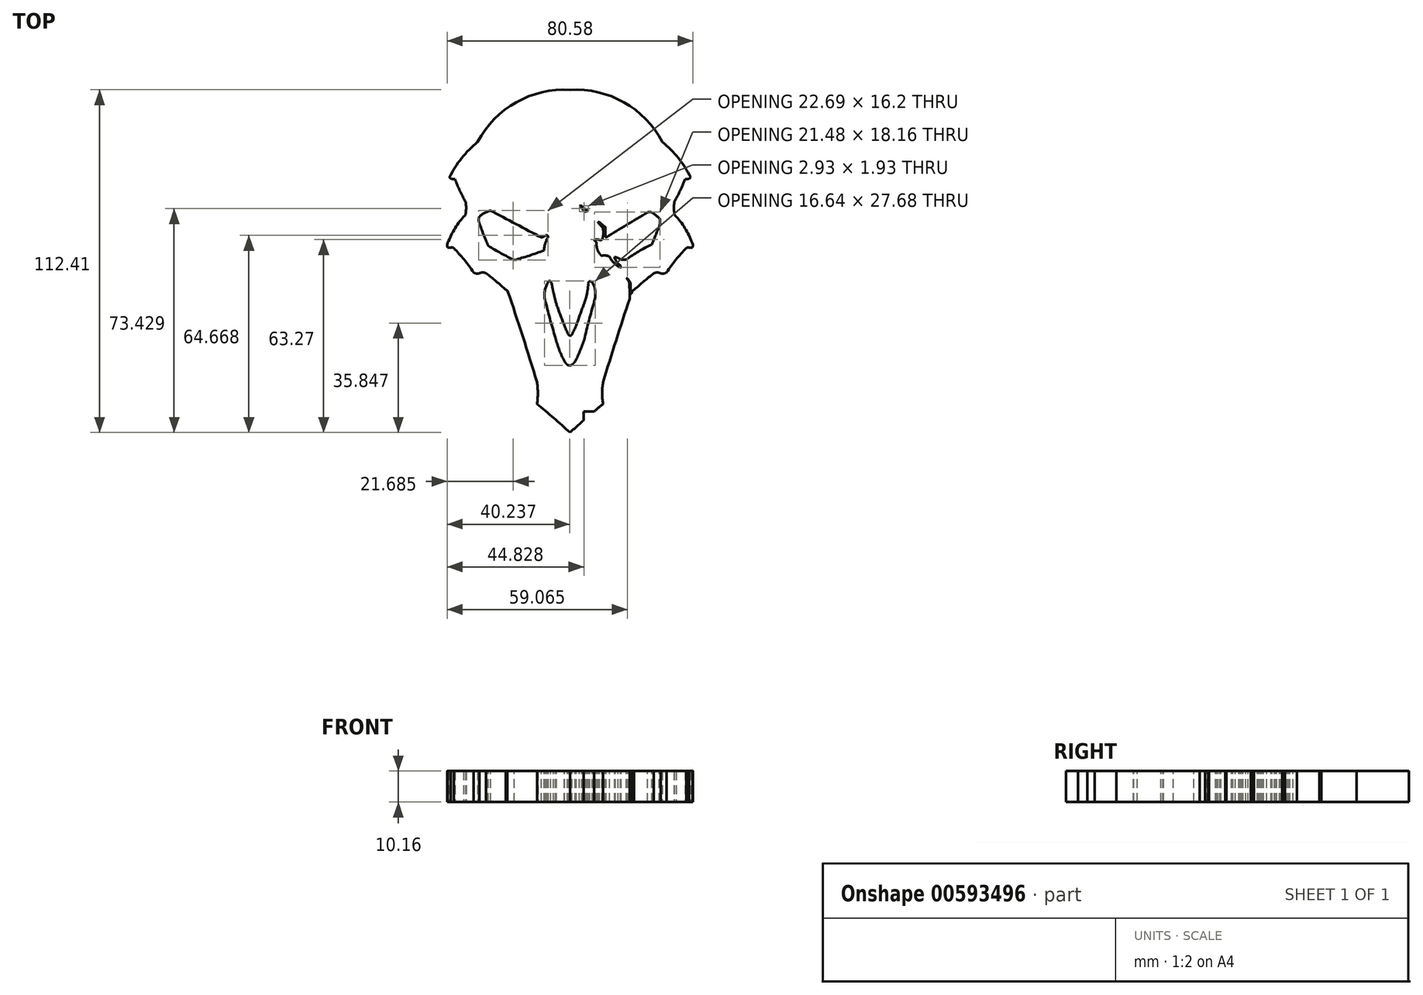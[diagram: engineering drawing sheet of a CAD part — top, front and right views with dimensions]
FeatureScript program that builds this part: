
annotation { "Feature Type Name" : "Feature", "Feature Type Description" : "" }
export const myFeature = defineFeature(function(context is Context, id is Id, definition is map)
    precondition{}
    {
        {
            var Q0;
            Q0=qCreatedBy(makeId("Top.planeOp"),FACE);
            var sketch = newSketch(context, id + "F0", { "sketchPlane" : qUnion([Q0])});
            skArc(sketch, "E0", {"start": v(-30.27, 46.68) * mm, "mid": v(-35.53, 41.4) * mm, "end": v(-39.5, 35.1) * mm});
            skArc(sketch, "E1", {"start": v(-39.5, 35.1) * mm, "mid": v(-38.7, 34.53) * mm, "end": v(-37.73, 34.53) * mm});
            skArc(sketch, "E2", {"start": v(-37.73, 34.53) * mm, "mid": v(-36.12, 30.74) * mm, "end": v(-34.24, 27.07) * mm});
            skArc(sketch, "E3", {"start": v(-34.24, 23.12) * mm, "mid": v(-34.05, 25.1) * mm, "end": v(-34.24, 27.07) * mm});
            skArc(sketch, "E4", {"start": v(-34.86, 22.24) * mm, "mid": v(-34.4, 22.58) * mm, "end": v(-34.24, 23.12) * mm});
            skArc(sketch, "E5", {"start": v(-38.1, 11.91) * mm, "mid": v(-38.57, 12.1) * mm, "end": v(-39.06, 12.04) * mm});
            skArc(sketch, "E6", {"start": v(-31.65, 3.94) * mm, "mid": v(-34.7, 8.07) * mm, "end": v(-38.1, 11.91) * mm});
            skArc(sketch, "E7", {"start": v(-34.86, 22.24) * mm, "mid": v(-38, 17.87) * mm, "end": v(-40.29, 12.99) * mm});
            skArc(sketch, "E8", {"start": v(-40.29, 12.99) * mm, "mid": v(-40.25, 12.5) * mm, "end": v(-40.1, 12.04) * mm});
            skArc(sketch, "E9", {"start": v(-40.1, 12.04) * mm, "mid": v(-39.58, 12.03) * mm, "end": v(-39.06, 12.04) * mm});
            skArc(sketch, "E10", {"start": v(-31.65, 3.94) * mm, "mid": v(-30.7, 3.53) * mm, "end": v(-29.68, 3.65) * mm});
            skArc(sketch, "E11", {"start": v(-27.5, 3.65) * mm, "mid": v(-28.59, 3.9) * mm, "end": v(-29.68, 3.65) * mm});
            skArc(sketch, "E12", {"start": v(-21.02, -1.81) * mm, "mid": v(-24.21, 0.97) * mm, "end": v(-27.5, 3.65) * mm});
            skArc(sketch, "E13", {"start": v(-20.5, -2.08) * mm, "mid": v(-20.73, -1.9) * mm, "end": v(-21.02, -1.81) * mm});
            skArc(sketch, "E14", {"start": v(-10.83, -32.15) * mm, "mid": v(-15.5, -17.06) * mm, "end": v(-20.5, -2.08) * mm});
            skArc(sketch, "E15", {"start": v(-10.83, -39.22) * mm, "mid": v(-10.55, -35.68) * mm, "end": v(-10.83, -32.15) * mm});
            skArc(sketch, "E16", {"start": v(0, -48.6) * mm, "mid": v(-5.35, -43.82) * mm, "end": v(-10.83, -39.22) * mm});
            skLineSegment(sketch, "E17", {"start": v(0, 63.77) * mm, "end": v(0, -48.6) * mm});
            skArc(sketch, "E18", {"start": v(0, 63.77) * mm, "mid": v(-17.65, 59.68) * mm, "end": v(-30.27, 46.68) * mm});
            skSolve(sketch);
        }
        {
            var Q0;
            Q0 = qSketchRegion(id + "F0", true);
            extrude(context, id + "F1", {"entities" : qUnion([Q0]), "depth" : 10.16 * mm, "offsetDistance" : 25.4 * mm});
        }
        {
            var Q0;
            Q0=makeQuery(id+"F1.opExtrude","SWEPT_BODY",BODY,{"disambiguationData":[OSD([sQuery(id+"F0.wireOp",EDGE,"E0"),sQuery(id+"F0.wireOp",EDGE,"E1"),sQuery(id+"F0.wireOp",EDGE,"E2"),sQuery(id+"F0.wireOp",EDGE,"E3"),sQuery(id+"F0.wireOp",EDGE,"E4"),sQuery(id+"F0.wireOp",EDGE,"E5"),sQuery(id+"F0.wireOp",EDGE,"E6"),sQuery(id+"F0.wireOp",EDGE,"E7"),sQuery(id+"F0.wireOp",EDGE,"E8"),sQuery(id+"F0.wireOp",EDGE,"E9"),sQuery(id+"F0.wireOp",EDGE,"E10"),sQuery(id+"F0.wireOp",EDGE,"E11"),sQuery(id+"F0.wireOp",EDGE,"E12"),sQuery(id+"F0.wireOp",EDGE,"E13"),sQuery(id+"F0.wireOp",EDGE,"E14"),sQuery(id+"F0.wireOp",EDGE,"E15"),sQuery(id+"F0.wireOp",EDGE,"E16"),sQuery(id+"F0.wireOp",EDGE,"E17"),sQuery(id+"F0.wireOp",EDGE,"E18")])]});
            var Q1;
            Q1=qCreatedBy(makeId("Right.planeOp"),FACE);
            mirror(context, id + "F2", {"operationType" : NewBodyOperationType.ADD, "entities" : qUnion([Q0]), "mirrorPlane" : qUnion([Q1])});
        }
        {
            var Q0;
            {var subQ0=makeQuery(id+"F1.opExtrude","CAP_FACE",FACE,{"disambiguationData":[OSD([sQuery(id+"F0.wireOp",EDGE,"E0"),sQuery(id+"F0.wireOp",EDGE,"E1"),sQuery(id+"F0.wireOp",EDGE,"E2"),sQuery(id+"F0.wireOp",EDGE,"E3"),sQuery(id+"F0.wireOp",EDGE,"E4"),sQuery(id+"F0.wireOp",EDGE,"E5"),sQuery(id+"F0.wireOp",EDGE,"E6"),sQuery(id+"F0.wireOp",EDGE,"E7"),sQuery(id+"F0.wireOp",EDGE,"E8"),sQuery(id+"F0.wireOp",EDGE,"E9"),sQuery(id+"F0.wireOp",EDGE,"E10"),sQuery(id+"F0.wireOp",EDGE,"E11"),sQuery(id+"F0.wireOp",EDGE,"E12"),sQuery(id+"F0.wireOp",EDGE,"E13"),sQuery(id+"F0.wireOp",EDGE,"E14"),sQuery(id+"F0.wireOp",EDGE,"E15"),sQuery(id+"F0.wireOp",EDGE,"E16"),sQuery(id+"F0.wireOp",EDGE,"E17"),sQuery(id+"F0.wireOp",EDGE,"E18")])],"isStart":false});Q0=makeQuery(id+"F2.boolean.opBoolean","MERGE",FACE,{"derivedFrom":[subQ0,makeQuery(id+"F2.opPattern","COPY",FACE,{"derivedFrom":subQ0,"instanceName":"1"})]});}
            var sketch = newSketch(context, id + "F3", { "sketchPlane" : qUnion([Q0])});
            skArc(sketch, "E19", {"start": v(-26, 24.18) * mm, "mid": v(-17.72, 19.77) * mm, "end": v(-9.44, 15.37) * mm});
            skArc(sketch, "E20", {"start": v(-9.44, 15.37) * mm, "mid": v(-8.67, 15.65) * mm, "end": v(-7.94, 16.04) * mm});
            skArc(sketch, "E21", {"start": v(-26.76, 12.61) * mm, "mid": v(-22.58, 10.17) * mm, "end": v(-18.26, 7.98) * mm});
            skArc(sketch, "E22", {"start": v(-29.69, 20.03) * mm, "mid": v(-28.33, 16.28) * mm, "end": v(-26.76, 12.61) * mm});
            skArc(sketch, "E23", {"start": v(-29.69, 22.27) * mm, "mid": v(-29.95, 21.15) * mm, "end": v(-29.69, 20.03) * mm});
            skArc(sketch, "E24", {"start": v(-26, 24.18) * mm, "mid": v(-27.96, 23.44) * mm, "end": v(-29.69, 22.27) * mm});
            skArc(sketch, "E25", {"start": v(-7.58, 16.16) * mm, "mid": v(-7.77, 16.1) * mm, "end": v(-7.94, 16.04) * mm});
            skArc(sketch, "E26", {"start": v(-7.58, 16.16) * mm, "mid": v(-7.47, 16.14) * mm, "end": v(-7.35, 16.16) * mm});
            skArc(sketch, "E27", {"start": v(-7.28, 15.37) * mm, "mid": v(-7.26, 15.77) * mm, "end": v(-7.35, 16.16) * mm});
            skArc(sketch, "E28", {"start": v(-7.28, 15.37) * mm, "mid": v(-8.16, 13.31) * mm, "end": v(-8.55, 11.1) * mm});
            skArc(sketch, "E29", {"start": v(-18.26, 7.98) * mm, "mid": v(-13.36, 9.42) * mm, "end": v(-8.55, 11.1) * mm});
            skSolve(sketch);
        }
        {
            var Q0;
            Q0 = qSketchRegion(id + "F3", true);
            extrude(context, id + "F4", {"entities" : qUnion([Q0]), "operationType" : NewBodyOperationType.REMOVE, "oppositeDirection" : true, "depth" : 25.4 * mm, "offsetDistance" : 25.4 * mm});
        }
        {
            var Q0;
            {var subQ0=makeQuery(id+"F1.opExtrude","CAP_FACE",FACE,{"disambiguationData":[OSD([sQuery(id+"F0.wireOp",EDGE,"E0"),sQuery(id+"F0.wireOp",EDGE,"E1"),sQuery(id+"F0.wireOp",EDGE,"E2"),sQuery(id+"F0.wireOp",EDGE,"E3"),sQuery(id+"F0.wireOp",EDGE,"E4"),sQuery(id+"F0.wireOp",EDGE,"E5"),sQuery(id+"F0.wireOp",EDGE,"E6"),sQuery(id+"F0.wireOp",EDGE,"E7"),sQuery(id+"F0.wireOp",EDGE,"E8"),sQuery(id+"F0.wireOp",EDGE,"E9"),sQuery(id+"F0.wireOp",EDGE,"E10"),sQuery(id+"F0.wireOp",EDGE,"E11"),sQuery(id+"F0.wireOp",EDGE,"E12"),sQuery(id+"F0.wireOp",EDGE,"E13"),sQuery(id+"F0.wireOp",EDGE,"E14"),sQuery(id+"F0.wireOp",EDGE,"E15"),sQuery(id+"F0.wireOp",EDGE,"E16"),sQuery(id+"F0.wireOp",EDGE,"E17"),sQuery(id+"F0.wireOp",EDGE,"E18")])],"isStart":false});Q0=makeQuery(id+"F2.boolean.opBoolean","MERGE",FACE,{"derivedFrom":[subQ0,makeQuery(id+"F2.opPattern","COPY",FACE,{"derivedFrom":subQ0,"instanceName":"1"})]});}
            var sketch = newSketch(context, id + "F5", { "sketchPlane" : qUnion([Q0])});
            skArc(sketch, "E30", {"start": v(25.42, 23.61) * mm, "mid": v(18.6, 19.55) * mm, "end": v(11.87, 15.37) * mm});
            skArc(sketch, "E31", {"start": v(26.78, 23.61) * mm, "mid": v(26.1, 23.76) * mm, "end": v(25.42, 23.61) * mm});
            skArc(sketch, "E32", {"start": v(29.26, 21.73) * mm, "mid": v(28.05, 22.71) * mm, "end": v(26.78, 23.61) * mm});
            skArc(sketch, "E33", {"start": v(29.5, 21.39) * mm, "mid": v(29.4, 21.57) * mm, "end": v(29.26, 21.73) * mm});
            skArc(sketch, "E34", {"start": v(29.5, 19.76) * mm, "mid": v(29.51, 20.58) * mm, "end": v(29.5, 21.39) * mm});
            skArc(sketch, "E35", {"start": v(26.78, 13.08) * mm, "mid": v(28.17, 16.4) * mm, "end": v(29.5, 19.76) * mm});
            skArc(sketch, "E36", {"start": v(26.78, 13.08) * mm, "mid": v(22.49, 10.8) * mm, "end": v(18.43, 8.13) * mm});
            skArc(sketch, "E37", {"start": v(16.8, 8.13) * mm, "mid": v(17.62, 8.07) * mm, "end": v(18.43, 8.13) * mm});
            skArc(sketch, "E38", {"start": v(16.8, 8.13) * mm, "mid": v(15.76, 8.64) * mm, "end": v(14.65, 8.96) * mm});
            skArc(sketch, "E39", {"start": v(12.98, 9) * mm, "mid": v(13.7, 7.88) * mm, "end": v(14.58, 6.88) * mm});
            skArc(sketch, "E40", {"start": v(12.1, 9.4) * mm, "mid": v(11.24, 9.46) * mm, "end": v(10.38, 9.4) * mm});
            skArc(sketch, "E41", {"start": v(9.5, 10.35) * mm, "mid": v(9.88, 9.82) * mm, "end": v(10.38, 9.4) * mm});
            skArc(sketch, "E42", {"start": v(8.7, 13.2) * mm, "mid": v(8.88, 11.72) * mm, "end": v(9.5, 10.35) * mm});
            skArc(sketch, "E43", {"start": v(8.7, 13.2) * mm, "mid": v(8.63, 13.72) * mm, "end": v(8.25, 14.08) * mm});
            skArc(sketch, "E44", {"start": v(8.07, 14.36) * mm, "mid": v(8.15, 14.2) * mm, "end": v(8.25, 14.08) * mm});
            skArc(sketch, "E45", {"start": v(8.07, 14.73) * mm, "mid": v(8.03, 14.54) * mm, "end": v(8.07, 14.36) * mm});
            skArc(sketch, "E46", {"start": v(14.9, 8.09) * mm, "mid": v(15.57, 7) * mm, "end": v(16.55, 6.16) * mm});
            skArc(sketch, "E47", {"start": v(16.55, 6.16) * mm, "mid": v(16.6, 5.84) * mm, "end": v(16.84, 5.6) * mm});
            skArc(sketch, "E48", {"start": v(15.76, 5.9) * mm, "mid": v(16.27, 5.66) * mm, "end": v(16.84, 5.6) * mm});
            skArc(sketch, "E49", {"start": v(14.58, 6.88) * mm, "mid": v(15.14, 6.35) * mm, "end": v(15.76, 5.9) * mm});
            skArc(sketch, "E50", {"start": v(10.45, 14.6) * mm, "mid": v(10.58, 14.76) * mm, "end": v(10.64, 14.94) * mm});
            skArc(sketch, "E51", {"start": v(10.64, 14.94) * mm, "mid": v(10.87, 16.03) * mm, "end": v(10.9, 17.14) * mm});
            skArc(sketch, "E52", {"start": v(10.9, 17.14) * mm, "mid": v(10.85, 17.89) * mm, "end": v(10.64, 18.61) * mm});
            skArc(sketch, "E53", {"start": v(10.64, 18.61) * mm, "mid": v(10, 19.4) * mm, "end": v(9.28, 20.13) * mm});
            skArc(sketch, "E54", {"start": v(9.2, 20.42) * mm, "mid": v(9.22, 20.27) * mm, "end": v(9.28, 20.13) * mm});
            skArc(sketch, "E55", {"start": v(9.2, 20.42) * mm, "mid": v(9.46, 20.35) * mm, "end": v(9.72, 20.42) * mm});
            skArc(sketch, "E56", {"start": v(9.72, 20.42) * mm, "mid": v(10.53, 19.58) * mm, "end": v(11.48, 18.92) * mm});
            skArc(sketch, "E57", {"start": v(11.59, 18.76) * mm, "mid": v(11.55, 18.85) * mm, "end": v(11.48, 18.92) * mm});
            skArc(sketch, "E58", {"start": v(11.74, 15.48) * mm, "mid": v(11.78, 15.4) * mm, "end": v(11.87, 15.37) * mm});
            skArc(sketch, "E59", {"start": v(11.59, 18.76) * mm, "mid": v(11.54, 17.12) * mm, "end": v(11.74, 15.48) * mm});
            skArc(sketch, "E60", {"start": v(9.51, 14.6) * mm, "mid": v(9.98, 14.5) * mm, "end": v(10.45, 14.6) * mm});
            skArc(sketch, "E61", {"start": v(9.51, 14.6) * mm, "mid": v(9.27, 14.67) * mm, "end": v(9.02, 14.7) * mm});
            skArc(sketch, "E62", {"start": v(8.48, 14.71) * mm, "mid": v(8.75, 14.65) * mm, "end": v(9.02, 14.7) * mm});
            skArc(sketch, "E63", {"start": v(8.07, 14.73) * mm, "mid": v(8.27, 14.69) * mm, "end": v(8.48, 14.71) * mm});
            skArc(sketch, "E64", {"start": v(14.65, 8.96) * mm, "mid": v(14.6, 8.78) * mm, "end": v(14.65, 8.6) * mm});
            skArc(sketch, "E65", {"start": v(14.65, 8.6) * mm, "mid": v(14.76, 8.34) * mm, "end": v(14.9, 8.09) * mm});
            skArc(sketch, "E66", {"start": v(12.98, 9) * mm, "mid": v(12.57, 9.26) * mm, "end": v(12.1, 9.4) * mm});
            skSolve(sketch);
        }
        {
            var Q0;
            Q0 = qSketchRegion(id + "F5", true);
            extrude(context, id + "F6", {"entities" : qUnion([Q0]), "operationType" : NewBodyOperationType.REMOVE, "oppositeDirection" : true, "depth" : 25.4 * mm, "offsetDistance" : 25.4 * mm});
        }
        {
            var Q0;
            Q0 = qSketchRegion(id + "F5", true);
            extrude(context, id + "F7", {"entities" : qUnion([Q0]), "operationType" : NewBodyOperationType.REMOVE, "oppositeDirection" : true, "depth" : 25.4 * mm, "offsetDistance" : 25.4 * mm});
        }
        {
            var Q0;
            {var subQ0=makeQuery(id+"F1.opExtrude","CAP_FACE",FACE,{"disambiguationData":[OSD([sQuery(id+"F0.wireOp",EDGE,"E0"),sQuery(id+"F0.wireOp",EDGE,"E1"),sQuery(id+"F0.wireOp",EDGE,"E2"),sQuery(id+"F0.wireOp",EDGE,"E3"),sQuery(id+"F0.wireOp",EDGE,"E4"),sQuery(id+"F0.wireOp",EDGE,"E5"),sQuery(id+"F0.wireOp",EDGE,"E6"),sQuery(id+"F0.wireOp",EDGE,"E7"),sQuery(id+"F0.wireOp",EDGE,"E8"),sQuery(id+"F0.wireOp",EDGE,"E9"),sQuery(id+"F0.wireOp",EDGE,"E10"),sQuery(id+"F0.wireOp",EDGE,"E11"),sQuery(id+"F0.wireOp",EDGE,"E12"),sQuery(id+"F0.wireOp",EDGE,"E13"),sQuery(id+"F0.wireOp",EDGE,"E14"),sQuery(id+"F0.wireOp",EDGE,"E15"),sQuery(id+"F0.wireOp",EDGE,"E16"),sQuery(id+"F0.wireOp",EDGE,"E17"),sQuery(id+"F0.wireOp",EDGE,"E18")])],"isStart":false});Q0=makeQuery(id+"F2.boolean.opBoolean","MERGE",FACE,{"derivedFrom":[subQ0,makeQuery(id+"F2.opPattern","COPY",FACE,{"derivedFrom":subQ0,"instanceName":"1"})]});}
            var sketch = newSketch(context, id + "F8", { "sketchPlane" : qUnion([Q0])});
            skArc(sketch, "E67", {"start": v(19.58, -4.75) * mm, "mid": v(19.54, -2.14) * mm, "end": v(19.42, 0.46) * mm});
            skArc(sketch, "E68", {"start": v(19.42, 0.46) * mm, "mid": v(19.15, 1.16) * mm, "end": v(18.68, 1.76) * mm});
            skArc(sketch, "E69", {"start": v(18.68, 2) * mm, "mid": v(18.66, 1.88) * mm, "end": v(18.68, 1.76) * mm});
            skArc(sketch, "E70", {"start": v(18.75, 2.17) * mm, "mid": v(18.7, 2.1) * mm, "end": v(18.68, 2) * mm});
            skArc(sketch, "E71", {"start": v(18.75, 2.17) * mm, "mid": v(18.8, 1.91) * mm, "end": v(19, 1.74) * mm});
            skArc(sketch, "E72", {"start": v(19.78, 0.52) * mm, "mid": v(19.41, 1.15) * mm, "end": v(19, 1.74) * mm});
            skArc(sketch, "E73", {"start": v(19.78, 0.52) * mm, "mid": v(19.85, -1.26) * mm, "end": v(20.03, -3.02) * mm});
            skArc(sketch, "E74", {"start": v(20.03, -3.02) * mm, "mid": v(20.05, -3.06) * mm, "end": v(20.08, -3.08) * mm});
            skArc(sketch, "E75", {"start": v(20.08, -3.08) * mm, "mid": v(20.16, -3.07) * mm, "end": v(20.22, -3) * mm});
            skArc(sketch, "E76", {"start": v(19.58, -4.75) * mm, "mid": v(24.58, -5.6) * mm, "end": v(20.22, -3) * mm});
            skSolve(sketch);
        }
        {
            var Q0;
            {var subQ0=makeQuery(id+"F1.opExtrude","CAP_FACE",FACE,{"disambiguationData":[OSD([sQuery(id+"F0.wireOp",EDGE,"E0"),sQuery(id+"F0.wireOp",EDGE,"E1"),sQuery(id+"F0.wireOp",EDGE,"E2"),sQuery(id+"F0.wireOp",EDGE,"E3"),sQuery(id+"F0.wireOp",EDGE,"E4"),sQuery(id+"F0.wireOp",EDGE,"E5"),sQuery(id+"F0.wireOp",EDGE,"E6"),sQuery(id+"F0.wireOp",EDGE,"E7"),sQuery(id+"F0.wireOp",EDGE,"E8"),sQuery(id+"F0.wireOp",EDGE,"E9"),sQuery(id+"F0.wireOp",EDGE,"E10"),sQuery(id+"F0.wireOp",EDGE,"E11"),sQuery(id+"F0.wireOp",EDGE,"E12"),sQuery(id+"F0.wireOp",EDGE,"E13"),sQuery(id+"F0.wireOp",EDGE,"E14"),sQuery(id+"F0.wireOp",EDGE,"E15"),sQuery(id+"F0.wireOp",EDGE,"E16"),sQuery(id+"F0.wireOp",EDGE,"E17"),sQuery(id+"F0.wireOp",EDGE,"E18")])],"isStart":false});Q0=makeQuery(id+"F2.boolean.opBoolean","MERGE",FACE,{"derivedFrom":[subQ0,makeQuery(id+"F2.opPattern","COPY",FACE,{"derivedFrom":subQ0,"instanceName":"1"})]});}
            var sketch = newSketch(context, id + "F9", { "sketchPlane" : qUnion([Q0])});
            skArc(sketch, "E77", {"start": v(3.88, 25.76) * mm, "mid": v(4.36, 25.2) * mm, "end": v(4.93, 24.73) * mm});
            skArc(sketch, "E78", {"start": v(4.93, 24.73) * mm, "mid": v(5.45, 24.54) * mm, "end": v(6, 24.5) * mm});
            skArc(sketch, "E79", {"start": v(4.68, 23.9) * mm, "mid": v(4.97, 23.88) * mm, "end": v(5.26, 23.9) * mm});
            skArc(sketch, "E80", {"start": v(4.68, 23.9) * mm, "mid": v(3.93, 24.9) * mm, "end": v(3.07, 25.8) * mm});
            skArc(sketch, "E81", {"start": v(3.07, 25.8) * mm, "mid": v(3.47, 25.74) * mm, "end": v(3.88, 25.76) * mm});
            skArc(sketch, "E82", {"start": v(6, 24.5) * mm, "mid": v(5.8, 24.24) * mm, "end": v(5.69, 23.95) * mm});
            skArc(sketch, "E83", {"start": v(5.69, 23.95) * mm, "mid": v(5.47, 23.94) * mm, "end": v(5.26, 23.9) * mm});
            skSolve(sketch);
        }
        {
            var Q0;
            Q0 = qSketchRegion(id + "F9", true);
            extrude(context, id + "F10", {"entities" : qUnion([Q0]), "operationType" : NewBodyOperationType.REMOVE, "oppositeDirection" : true, "depth" : 25.4 * mm, "offsetDistance" : 25.4 * mm});
        }
        {
            var Q0;
            {var subQ20=sQuery(id+"F8.wireOp",EDGE,"E67");Q0=makeQuery(id+"F8.imprint","IMPRINT",FACE,{"disambiguationData":[TD([[makeQuery(id+"F8.imprint","IMPRINT",EDGE,{"derivedFrom":subQ20}),1.0]])]});}
            var sketch = newSketch(context, id + "F11", { "sketchPlane" : qUnion([Q0])});
            skArc(sketch, "E84", {"start": v(-6.35, 0.89) * mm, "mid": v(-6.69, 1.1) * mm, "end": v(-7.05, 0.93) * mm});
            skArc(sketch, "E85", {"start": v(-7.05, 0.93) * mm, "mid": v(-8.21, -1.83) * mm, "end": v(-8.25, -4.82) * mm});
            skArc(sketch, "E86", {"start": v(-8.25, -4.82) * mm, "mid": v(-6.62, -11.16) * mm, "end": v(-4.78, -17.44) * mm});
            skArc(sketch, "E87", {"start": v(-4.78, -17.44) * mm, "mid": v(-3.54, -21.47) * mm, "end": v(-1.75, -25.28) * mm});
            skArc(sketch, "E88", {"start": v(-1.75, -25.28) * mm, "mid": v(-1.37, -25.86) * mm, "end": v(-0.9, -26.35) * mm});
            skArc(sketch, "E89", {"start": v(-0.9, -26.35) * mm, "mid": v(-0.13, -26.59) * mm, "end": v(0.64, -26.35) * mm});
            skArc(sketch, "E90", {"start": v(0.64, -26.35) * mm, "mid": v(1.2, -25.84) * mm, "end": v(1.7, -25.28) * mm});
            skArc(sketch, "E91", {"start": v(1.7, -25.28) * mm, "mid": v(3.44, -21.43) * mm, "end": v(4.85, -17.44) * mm});
            skArc(sketch, "E92", {"start": v(8.19, -4.82) * mm, "mid": v(6.4, -11.1) * mm, "end": v(4.85, -17.44) * mm});
            skArc(sketch, "E93", {"start": v(8.19, -4.82) * mm, "mid": v(8.27, -3.16) * mm, "end": v(8.19, -1.5) * mm});
            skArc(sketch, "E94", {"start": v(8.19, -1.5) * mm, "mid": v(7.82, -0.38) * mm, "end": v(7.27, 0.67) * mm});
            skArc(sketch, "E95", {"start": v(7.27, 0.67) * mm, "mid": v(6.93, 0.9) * mm, "end": v(6.55, 1.01) * mm});
            skArc(sketch, "E96", {"start": v(5.65, -2.47) * mm, "mid": v(5.9, -1.06) * mm, "end": v(5.93, 0.36) * mm});
            skArc(sketch, "E97", {"start": v(4.5, -6.68) * mm, "mid": v(5.18, -4.6) * mm, "end": v(5.65, -2.47) * mm});
            skArc(sketch, "E98", {"start": v(4.5, -6.68) * mm, "mid": v(3.23, -10.02) * mm, "end": v(2.08, -13.4) * mm});
            skArc(sketch, "E99", {"start": v(0.57, -16.55) * mm, "mid": v(1.35, -14.98) * mm, "end": v(2.08, -13.4) * mm});
            skArc(sketch, "E100", {"start": v(-0.45, -16.55) * mm, "mid": v(0.06, -16.81) * mm, "end": v(0.57, -16.55) * mm});
            skArc(sketch, "E101", {"start": v(-1.88, -13.4) * mm, "mid": v(-1.23, -15) * mm, "end": v(-0.45, -16.55) * mm});
            skArc(sketch, "E102", {"start": v(-4.4, -6.68) * mm, "mid": v(-3.18, -10.05) * mm, "end": v(-1.88, -13.4) * mm});
            skArc(sketch, "E103", {"start": v(-5.5, -2.47) * mm, "mid": v(-4.97, -4.58) * mm, "end": v(-4.4, -6.68) * mm});
            skArc(sketch, "E104", {"start": v(-5.97, -0.02) * mm, "mid": v(-5.74, -1.24) * mm, "end": v(-5.5, -2.47) * mm});
            skArc(sketch, "E105", {"start": v(-5.97, -0.02) * mm, "mid": v(-6.1, 0.46) * mm, "end": v(-6.35, 0.89) * mm});
            skArc(sketch, "E106", {"start": v(6.55, 1.01) * mm, "mid": v(6.15, 0.77) * mm, "end": v(5.93, 0.36) * mm});
            skSolve(sketch);
        }
        {
            var Q0;
            Q0 = qSketchRegion(id + "F11", true);
            extrude(context, id + "F12", {"entities" : qUnion([Q0]), "operationType" : NewBodyOperationType.REMOVE, "oppositeDirection" : true, "depth" : 25.4 * mm, "offsetDistance" : 25.4 * mm});
        }
        {
            var Q0;
            {var subQ0=makeQuery(id+"F1.opExtrude","CAP_FACE",FACE,{"disambiguationData":[OSD([sQuery(id+"F0.wireOp",EDGE,"E0"),sQuery(id+"F0.wireOp",EDGE,"E1"),sQuery(id+"F0.wireOp",EDGE,"E2"),sQuery(id+"F0.wireOp",EDGE,"E3"),sQuery(id+"F0.wireOp",EDGE,"E4"),sQuery(id+"F0.wireOp",EDGE,"E5"),sQuery(id+"F0.wireOp",EDGE,"E6"),sQuery(id+"F0.wireOp",EDGE,"E7"),sQuery(id+"F0.wireOp",EDGE,"E8"),sQuery(id+"F0.wireOp",EDGE,"E9"),sQuery(id+"F0.wireOp",EDGE,"E10"),sQuery(id+"F0.wireOp",EDGE,"E11"),sQuery(id+"F0.wireOp",EDGE,"E12"),sQuery(id+"F0.wireOp",EDGE,"E13"),sQuery(id+"F0.wireOp",EDGE,"E14"),sQuery(id+"F0.wireOp",EDGE,"E15"),sQuery(id+"F0.wireOp",EDGE,"E16"),sQuery(id+"F0.wireOp",EDGE,"E17"),sQuery(id+"F0.wireOp",EDGE,"E18")])],"isStart":false});Q0=makeQuery(id+"F2.boolean.opBoolean","MERGE",FACE,{"derivedFrom":[subQ0,makeQuery(id+"F2.opPattern","COPY",FACE,{"derivedFrom":subQ0,"instanceName":"1"})]});}
            var sketch = newSketch(context, id + "F13", { "sketchPlane" : qUnion([Q0])});
            skLineSegment(sketch, "E107", {"start": v(4.41, -44.64) * mm, "end": v(4.41, -41.69) * mm});
            skLineSegment(sketch, "E108", {"start": v(4.41, -41.69) * mm, "end": v(7.85, -41.69) * mm});
            skArc(sketch, "E109", {"start": v(4.41, -44.64) * mm, "mid": v(7.42, -44.66) * mm, "end": v(7.85, -41.69) * mm});
            skSolve(sketch);
        }
        {
            var Q0;
            Q0 = qSketchRegion(id + "F13", true);
            extrude(context, id + "F14", {"entities" : qUnion([Q0]), "operationType" : NewBodyOperationType.REMOVE, "oppositeDirection" : true, "depth" : 25.4 * mm, "offsetDistance" : 25.4 * mm});
        }
        {
            var Q0;
            Q0 = qSketchRegion(id + "F8", true);
            extrude(context, id + "F15", {"entities" : qUnion([Q0]), "operationType" : NewBodyOperationType.REMOVE, "oppositeDirection" : true, "depth" : 25.4 * mm, "offsetDistance" : 25.4 * mm});
        }
    });
